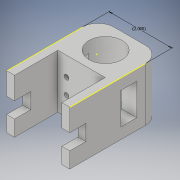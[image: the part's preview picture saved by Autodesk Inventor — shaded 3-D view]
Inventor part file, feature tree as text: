
AUTODESK INVENTOR PART (.ipt)
format: ipt  version: 2017 (Build 210142000, 142)  size: 259,584 bytes
history: native  units: in
note: dims shown in document units (in); Inventor stores cm internally (conversion verified against a paired STEP export)
features: sketch x13, extrude x7, hole x2, fillet x1, thicken_offset x1
ambient origin geometry x8: Origin, YZ Plane, XZ Plane, XY Plane, X Axis, Y Axis, Z Axis, Center Point
bodies: Solid1 (feature_tree)
feature tree (24):
  extrude  "Extrusion1"  Depth=1.0in
  extrude  "Extrusion2"  Depth=0.35in
  hole  "Hole1"  [1 undecoded]
  extrude  "Extrusion3"  Depth=0.15in
  extrude  "Extrusion4"  Depth=0.15in
  sketch  "Sketch6"  dims[d18=0.15in d19=0.15in]
  extrude  "Extrusion5"  Depth=0.15in
  hole  "Hole2"  [1 undecoded]
  fillet  "Fillet3"  Radius=0.35in
  extrude  "Extrusion6"  Depth=2.0in
  extrude  "Extrusion7"  Depth=1.5in
  thicken_offset  "Thicken1"
  sketch  "Sketch11"  dims[d30=0.25in]
  sketch  "Sketch12"  dims[d31=0.25in d32=0.0in]
  sketch  "Sketch13"  dims[d33=0.525in d34=0.4in d35=0.525in d36=0.6in d37=0.525in d38=0.4in d39=0.6in d40=0.525in d41=0.15in d42=0.75in d43=0.375in d44=0.25in d45=0.5635in d46=1.0in d47=0.8108in d48=0.25in d49=0.25in d50=1.375in d51=0.0in d52=0.5in d53=0.5in d54=1.375in d55=0.0in d58=1.275in d59=0.0in d60=0.7625in d61=1.0in d62=0.7625in d63=1.0in d64=1.055in d65=0.75in d66=0.375in d67=0.25in d68=0.5635in d69=1.0in d70=0.8108in d71=0.5in d73=0.6in d74=0.525in d75=0.5in d76=0.95in d77=0.95in d78=0.15in d79=0.15in d80=0.5in d81=0.15in d82=0.4in d83=0.95in d84=0.75in d85=0.0in d86=0.5in d87=1.0in d88=0.25in d89=1.275in d90=0.0in d91=0.15in d92=0.2in d93=0.2in d95=2.0in]
  sketch  "Sketch1"  dims[d0=1.25in d1=1.0in]
  sketch  "Sketch2"  dims[d10=0.15in d11=0.35in]
  sketch  "Sketch3"  dims[d12=0.15in d13=0.15in]
  sketch  "Sketch4"  dims[d14=0.35in d15=0.15in]
  sketch  "Sketch5"  dims[d16=0.15in d17=0.15in]
  sketch  "Sketch7"  dims[d20=0.15in d21=0.15in d22=0.35in]
  sketch  "Sketch8"  dims[d23=0.25in d24=0.0in d25=2.0in]
  sketch  "Sketch9"  dims[d26=1.5in d27=0.375in]
  sketch  "Sketch10"  dims[d29=0.375in]
note: 2 required parameter values undecoded (feature->parameter linkage not recoverable at this tier; creation-order binding heuristic only, values carry confidence <= 0.55)
